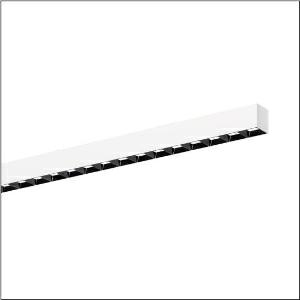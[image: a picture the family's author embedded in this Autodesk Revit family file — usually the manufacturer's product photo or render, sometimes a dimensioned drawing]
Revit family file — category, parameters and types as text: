
# Revit family: silica_r__21_51mx22dc3awb_a852
name_source: partatom
category: Lighting Fixtures
units: mm (PartAtom-declared; Revit-internal decimal feet)

## family parameters
Cut with Voids When Loaded = No
Host = Face
Light Source = No
Part Type = Normal
Room Calculation Point = No
Round Connector Dimension = Use Diameter
Shared = No

## types (1)
- --- (1 x LED, 10800 lm, 69.2 W, 3000K)
    Apparent Load = 69 VA
    CIE Flux Codes = 86 100 100 100 100
    Color Rendering = 80
    Color Temperature = 3000K
    Default Elevation = 1800 mm
    Description = Silica® 21, office luminaire, primary light control with darklight reflector, of PMMA, black, CAT 2 (L<= 3000cd/m²), light emission: direct distribution, primary light characteristic: symmetric, installation type: surface-mounted, LED, rated luminous flux: 10.800lm, luminous efficacy: 156lm/W, light colour: 830, colour temperature: 3000K, with terminal, 3+2-pole, max. 2.5mm², mains connection: 220..240V, AC, 50/60Hz, rated input power: 69.2W, luminaire housing, of aluminium, traffic white (RAL 9016), length: 3.004mm, width: 53mm, height: 53mm, protection rating (complete): IP20, insulation class (complete): insulation class I (protective earthing), certification: CE, permissible operating ambient temperature: 0..+35°C, standard: EN 50419, packaging unit: 1 piece
    Height = 0 mm  [stored 0 ft]
    Lamp = 1 x LED
    Lamp Light Flux = 10800 lm
    Lamp Power = 69.2 W
    Lamp count = 1
    Length = 3004 mm
    Luminous efficacy = 156 lm/W
    Manufacturer = Siteco
    ModVariant = No
    Model = 51MX22DC3AWB
    Mounting Place = Ceiling
    Mounting Type = Recessed
    Number of Poles = 1
    OnlyDefault = Yes
    Power Factor = 1
    Product Name = Silica® 21
    Product group = office luminaire | ceiling recessed
    ProductGroupID = 401
    Protection Class = Protection class I
    Protection Degree = IP 20
    RLX_Detail_Level = 1
    RLX_Emergency_Light_Flux = 0 lm
    RLX_Emergency_Type = 0
    RLX_Emergency_Type_DB = No
    RlxData = <blob elided: 62377 chars, md5=ebafde76>
    Socket = socket
    Standby Power = 0 W
    System Light Flux = 10800 lm
    System Power = 69 W
    Type Comments = factory setting: luminous flux: 100 % | dim-lin: 254 | 392 mA
    Type Image = l_1297779.jpg
    URL = http://relux.com
    VarID = @adj_056291
    Voltage = 0 V
    Weight = 0.00 kg
    Width = 53 mm

note: [stored X ft] marks values corroborated as IEEE doubles in the binary element streams (Revit-internal decimal feet)

## geometry (parser evidence)
native form markers: Blend x4, Sweep x9
no freeform markers — native parametric forms only
